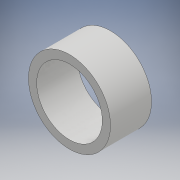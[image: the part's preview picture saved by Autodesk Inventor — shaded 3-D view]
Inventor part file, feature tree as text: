
AUTODESK INVENTOR PART (.ipt)
format: ipt  version: 2018.2 (Build 222227000, 227)  size: 101,376 bytes
history: native  units: mm
features: other x1, extrude x1, sketch x1
ambient origin geometry x8: Origin, YZ Plane, XZ Plane, XY Plane, X Axis, Y Axis, Z Axis, Center Point
bodies: Body1 (feature_tree)
feature tree (3):
  other  "ソリッド1"
  extrude  "押し出し1"  Depth=10.0mm
  sketch  "スケッチ1"
